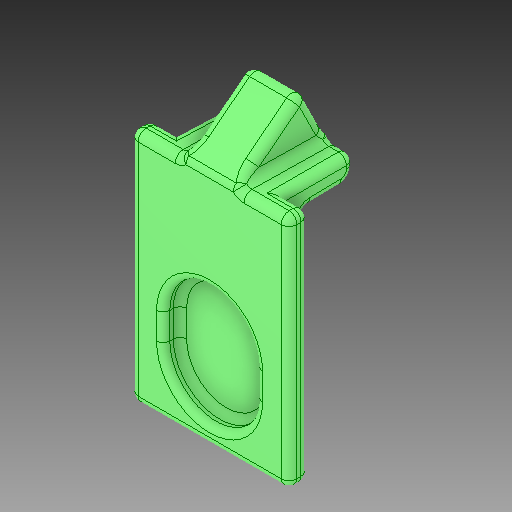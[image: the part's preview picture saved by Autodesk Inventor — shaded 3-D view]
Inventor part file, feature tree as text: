
AUTODESK INVENTOR PART (.ipt)
format: ipt  version: 2017 (Build 210142000, 142)  size: 278,016 bytes
history: native  units: in
note: dims shown in document units (in); Inventor stores cm internally (conversion verified against a paired STEP export)
features: fillet x1
ambient origin geometry x8: Origin, YZ Plane, XZ Plane, XY Plane, X Axis, Y Axis, Z Axis, Center Point
bodies: Solid1 (feature_tree)
feature tree (1):
  fillet  "Fillet4"  [1 undecoded]
note: 1 required parameter value undecoded (feature->parameter linkage not recoverable at this tier; creation-order binding heuristic only, values carry confidence <= 0.55)
